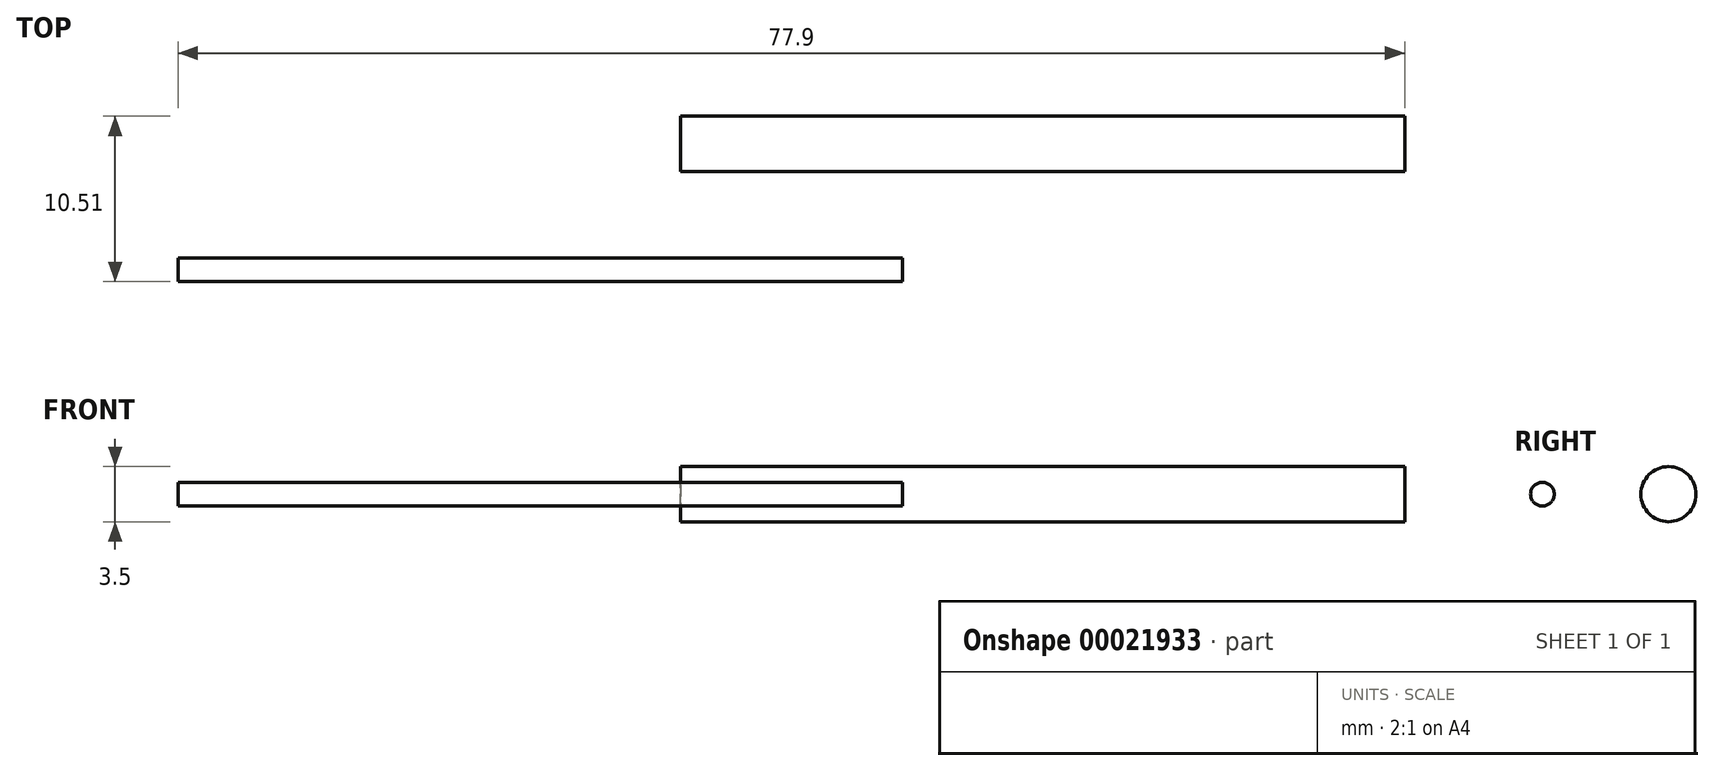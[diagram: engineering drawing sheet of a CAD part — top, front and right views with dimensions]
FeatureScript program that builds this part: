
annotation { "Feature Type Name" : "Feature", "Feature Type Description" : "" }
export const myFeature = defineFeature(function(context is Context, id is Id, definition is map)
    precondition{}
    {
        {
            var Q0;
            Q0=qCreatedBy(makeId("Top.planeOp"),FACE);
            var sketch = newSketch(context, id + "F0", { "sketchPlane" : qUnion([Q0])});
            skLineSegment(sketch, "E0.bottom", {"start": v(3.28, 13.93) * mm, "end": v(49.28, 13.93) * mm});
            skLineSegment(sketch, "E0.top", {"start": v(3.28, 12.18) * mm, "end": v(49.28, 12.18) * mm});
            skLineSegment(sketch, "E0.left", {"start": v(3.28, 13.93) * mm, "end": v(3.28, 12.18) * mm});
            skLineSegment(sketch, "E0.right", {"start": v(49.28, 13.93) * mm, "end": v(49.28, 12.18) * mm});
            skLineSegment(sketch, "E1.bottom", {"start": v(-28.62, 4.92) * mm, "end": v(17.38, 4.92) * mm});
            skLineSegment(sketch, "E1.top", {"start": v(-28.62, 4.17) * mm, "end": v(17.38, 4.17) * mm});
            skLineSegment(sketch, "E1.left", {"start": v(-28.62, 4.92) * mm, "end": v(-28.62, 4.17) * mm});
            skLineSegment(sketch, "E1.right", {"start": v(17.38, 4.92) * mm, "end": v(17.38, 4.17) * mm});
            skSolve(sketch);
        }
        {
            var Q0;
            Q0=makeQuery(id+"F0.imprint","IMPRINT",FACE,{"disambiguationData":[TD([[makeQuery(id+"F0.imprint","IMPRINT",EDGE,{"derivedFrom":sQuery(id+"F0.wireOp",EDGE,"E0.bottom")}),-1.0]])]});
            var Q1;
            Q1=sQuery(id+"F0.wireOp",EDGE,"E0.top");
            revolve(context, id + "F1", {"entities" : qUnion([Q0]), "axis" : qUnion([Q1]), "revolveType" : RevolveType.FULL});
        }
        {
            var Q0;
            Q0=makeQuery(id+"F0.imprint","IMPRINT",FACE,{"disambiguationData":[TD([[makeQuery(id+"F0.imprint","IMPRINT",EDGE,{"derivedFrom":sQuery(id+"F0.wireOp",EDGE,"E1.bottom")}),-1.0]])]});
            var Q1;
            Q1=sQuery(id+"F0.wireOp",EDGE,"E1.top");
            revolve(context, id + "F2", {"entities" : qUnion([Q0]), "axis" : qUnion([Q1]), "revolveType" : RevolveType.FULL});
        }
    });
